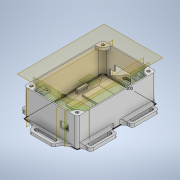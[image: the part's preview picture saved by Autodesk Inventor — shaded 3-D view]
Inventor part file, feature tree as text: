
AUTODESK INVENTOR PART (.ipt)
format: ipt  version: 2021 (Build 250183000, 183)  size: 672,256 bytes
history: native  units: in
note: dims shown in document units (in); Inventor stores cm internally (conversion verified against a paired STEP export)
features: extrude x26, sketch x25, mirror x9, fillet x7, plane x6, chamfer x2, reference x2, other x2
ambient origin geometry x8: Origin, YZ Plane, XZ Plane, XY Plane, X Axis, Y Axis, Z Axis, Center Point
bodies: Solid1 (feature_tree)
feature tree (79):
  sketch  "Sketch1"  dims[d0=3.937in d1=5.9055in]
  extrude  "Extrusion1"  Depth=5.9055in
  extrude  "Extrusion2"  Depth=2.1654in TaperAngle=0.0deg
  sketch  "Sketch2"  dims[d2=0.0787in d3=2.1654in d4=0.0in]
  plane  "Work Plane1"
  extrude  "Extrusion3"  [1 undecoded]
  plane  "Work Plane3"
  plane  "Work Plane4"
  extrude  "Extrusion21"  Depth=1.2598in
  extrude  "Extrusion6"  Depth=0.7087in
  extrude  "Extrusion7"  Depth=2.8346in
  extrude  "Extrusion8"  Depth=0.7874in
  mirror  "Mirror1"
  plane  "Work Plane5"
  extrude  "Extrusion9"  Depth=1.378in
  extrude  "Extrusion10"  Depth=0.0906in
  extrude  "Extrusion11"  Depth=0.0866in
  chamfer  "Chamfer1"  Distance=0.5933in
  extrude  "Extrusion14"  Depth=0.1575in TaperAngle=45.0deg
  extrude  "Extrusion15"  Depth=0.0906in
  extrude  "Extrusion16"  Depth=1.378in
  plane  "Work Plane7"
  mirror  "Mirror2"
  extrude  "Extrusion17"  Depth=0.0866in
  plane  "Work Plane8"
  extrude  "Extrusion19"  Depth=0.5933in
  mirror  "Mirror3"
  mirror  "Mirror4"
  fillet  "Fillet1"  Radius=0.5933in
  extrude  "Extrusion20"  Depth=0.3937in
  mirror  "Mirror5"
  extrude  "Extrusion22"  Depth=0.3937in
  fillet  "Fillet3"  Radius=0.2697in
  mirror  "Mirror6"
  mirror  "Mirror7"
  extrude  "Extrusion23"  Depth=0.0591in TaperAngle=0.0deg
  extrude  "Extrusion24"  Depth=0.1969in TaperAngle=0.0deg
  extrude  "Extrusion25"  Depth=0.5512in
  sketch  "Sketch43"  dims[d86=0.5906in d87=0.3937in d88=0.2697in d89=0.0in]
  extrude  "Extrusion26"  Depth=0.1299in
  extrude  "Extrusion27"  Depth=0.1969in
  extrude  "Extrusion28"  Depth=0.0157in
  extrude  "Extrusion29"  Depth=0.0157in
  extrude  "Extrusion30"  Depth=0.9055in
  extrude  "Extrusion31"  Depth=0.9055in
  mirror  "Mirror8"
  mirror  "Mirror9"
  chamfer  "Chamfer2"  [1 undecoded]
  fillet  "Fillet4"  Radius=1.8898in
  fillet  "Fillet5"  Radius=1.6535in
  fillet  "Fillet6"  Radius=0.2756in
  fillet  "Fillet7"  Radius=0.2362in
  fillet  "Fillet8"  Radius=1.6929in
  sketch  "Sketch6"  dims[d5=0.0787in d6=0.0in d7=-1.5748in]
  sketch  "Sketch11"  dims[d15=1.378in d16=1.2598in]
  sketch  "Sketch13"  dims[d17=1.0236in d18=0.7087in]
  sketch  "Sketch19"  dims[d19=0.1181in d20=0.0in d21=2.8346in]
  sketch  "Sketch20"  dims[d22=0.7087in d31=3.0in d42=0.7874in]
  sketch  "Sketch27"  dims[d43=0.4606in d44=1.378in]
  sketch  "Sketch29"  dims[d45=0.0906in d46=0.3819in]
  sketch  "Sketch30"  dims[d47=0.6327in d48=0.0in d49=0.0866in]
  sketch  "Sketch31"  dims[d50=0.4409in]
  sketch  "Sketch35"  dims[d51=0.3236in d52=0.5933in d53=0.0in]
  sketch  "Sketch36"  dims[d55=0.5933in d56=0.0in d57=0.1575in d58=0.0787in d59=45.0deg]
  sketch  "Sketch37"  dims[d63=0.7874in d64=0.0906in]
  reference  "Reference17"
  sketch  "Sketch38"  dims[d65=0.4606in d66=1.378in]
  sketch  "Sketch39"  dims[d67=0.6327in d68=0.0in d69=0.0866in]
  sketch  "Sketch40"  dims[d70=0.4409in d71=0.3236in d72=0.5933in d73=0.0in]
  sketch  "Sketch42"  dims[d75=0.5933in d76=0.0in d85=0.3937in]
  reference  "Reference21"
  sketch  "Sketch44"  dims[d90=0.1496in d91=0.0591in d92=0.0in]
  sketch  "Sketch45"  dims[d93=0.0906in d94=0.1969in d95=0.0in]
  sketch  "Sketch46"  dims[d96=0.689in d98=0.5512in]
  sketch  "Sketch47"  dims[d99=0.2362in d100=0.0in d106=0.1299in]
  sketch  "Sketch48"  dims[d107=0.0in d108=0.0in d109=0.1969in]
  sketch  "Sketch49"  dims[d110=0.1969in d111=0.0in d112=0.0157in d113=0.0157in d114=0.9055in d115=0.9055in d116=0.0in d117=1.8898in d120=1.6535in d121=0.2756in d123=0.2362in d124=1.6929in d125=0.1969in d126=2.0866in d127=0.3937in d129=0.2756in d130=0.1969in d131=0.2362in d132=0.0in d133=0.1969in d136=0.315in d137=0.315in d138=2.3622in d139=0.1969in d140=4.1126in d141=0.1752in d142=0.0in d143=0.1728in d144=0.1728in d145=0.0591in d146=0.0in d147=0.0197in d148=0.1181in d149=0.7874in d150=0.315in d151=0.0in d152=0.0591in d153=0.0in d154=0.315in d155=0.315in d156=0.9843in d157=0.7874in d158=0.2697in d159=0.0in d160=0.0906in d161=0.0906in d162=0.2362in d163=0.0in d164=0.1705in d165=0.1705in d166=0.0787in d167=0.0in d168=0.0917in d169=0.0917in d170=0.2362in d171=0.0in d172=0.2362in d173=0.1063in d174=0.0in d175=0.1575in d176=0.1969in d177=0.0787in d178=45.0deg d179=0.315in d180=0.315in d181=0.1969in d182=0.7874in d183=0.1969in d184=0.0394in d185=0.0in d186=0.0394in d187=0.0394in d188=0.4724in d189=0.0394in d190=0.0in d191=0.0394in d192=0.0394in d193=0.4724in d194=0.1181in]
  other  "Chestbox_with_electronical_devices.iam"
  other  "ArduinoMega_STEP_AP203:1"
note: 2 required parameter values undecoded (feature->parameter linkage not recoverable at this tier; creation-order binding heuristic only, values carry confidence <= 0.55)
